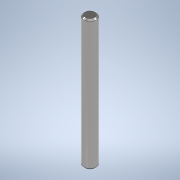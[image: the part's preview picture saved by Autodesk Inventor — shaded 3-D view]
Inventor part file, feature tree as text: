
AUTODESK INVENTOR PART (.ipt)
format: ipt  version: 2021 (Build 250183000, 183)  size: 95,744 bytes
history: native  units: mm
features: extrude x1, chamfer x1, sketch x1
ambient origin geometry x8: Origin, YZ Plane, XZ Plane, XY Plane, X Axis, Y Axis, Z Axis, Center Point
bodies: Solid1 (feature_tree)
feature tree (3):
  extrude  "Extrusion1"  Depth=84.5mm TaperAngle=0.0deg
  chamfer  "Chamfer1"  Distance=1.0mm Angle=45.0deg
  sketch  "Sketch1"  dims[d0=8.0mm d1=84.5mm d2=0.0mm d3=1.0mm d4=2.0mm d5=45.0deg]
